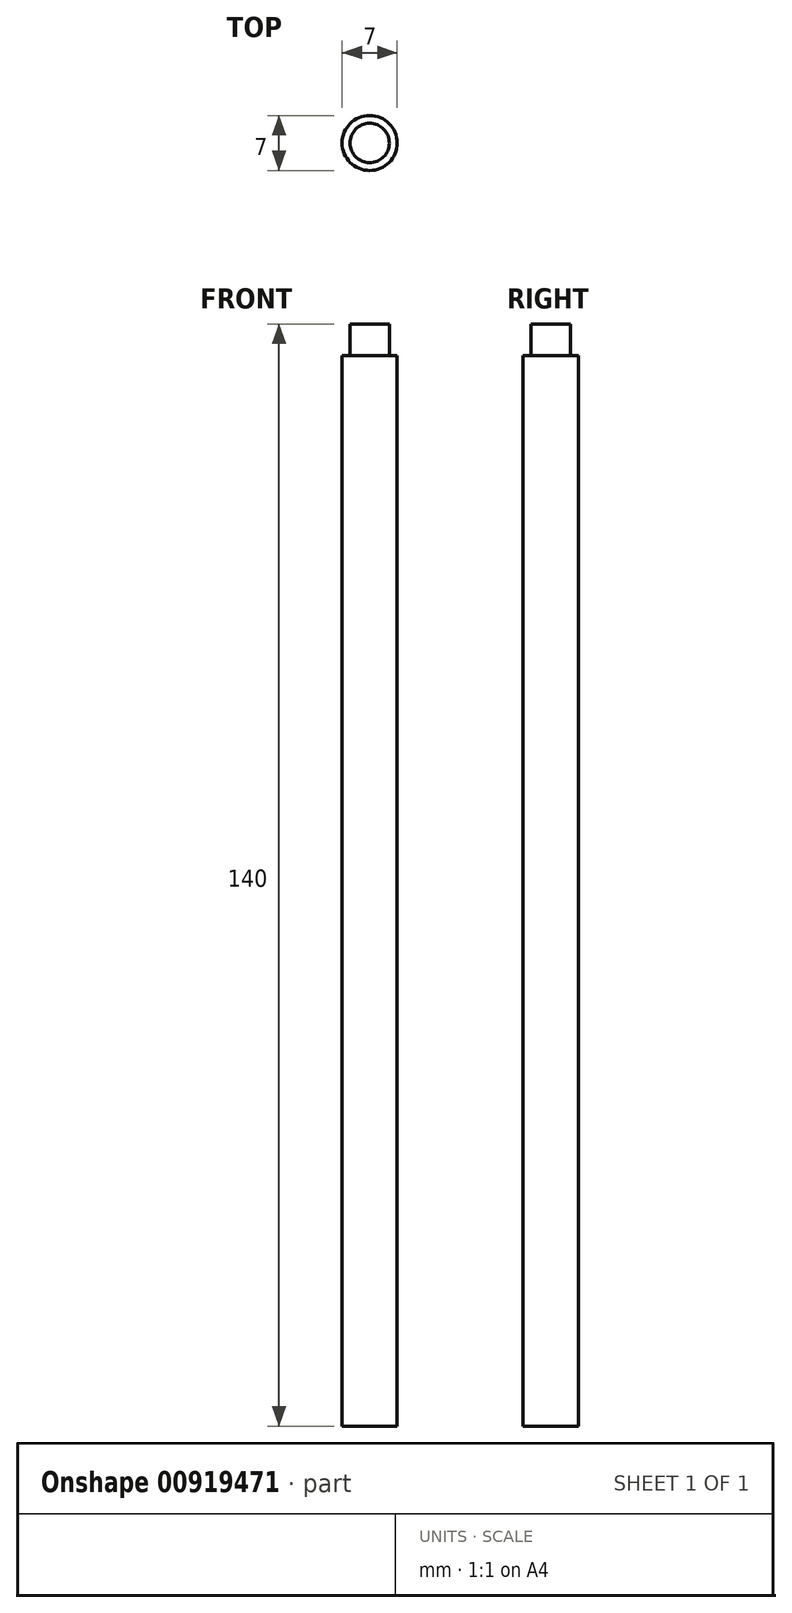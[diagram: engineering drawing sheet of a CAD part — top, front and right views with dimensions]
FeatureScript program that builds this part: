
annotation { "Feature Type Name" : "Feature", "Feature Type Description" : "" }
export const myFeature = defineFeature(function(context is Context, id is Id, definition is map)
    precondition{}
    {
        {
            var Q0;
            Q0=qCreatedBy(makeId("Top.planeOp"),FACE);
            var sketch = newSketch(context, id + "F0", { "sketchPlane" : qUnion([Q0])});
            skCircle(sketch, "E0", {"center": v(0, 0) * mm, "radius": 3.5 * mm});
            skSolve(sketch);
        }
        {
            var Q0;
            Q0 = qSketchRegion(id + "F0", true);
            extrude(context, id + "F1", {"entities" : qUnion([Q0]), "depth" : 140 * mm, "offsetDistance" : 25 * mm, "symmetric" : true});
        }
        {
            var Q0;
            Q0=makeQuery(id+"F1.opExtrude","CAP_FACE",FACE,{"disambiguationData":[OSD([sQuery(id+"F0.wireOp",EDGE,"E0")])],"isStart":false});
            var sketch = newSketch(context, id + "F2", { "sketchPlane" : qUnion([Q0])});
            skCircle(sketch, "E1", {"center": v(0, 0) * mm, "radius": 3.5 * mm});
            skCircle(sketch, "E2", {"center": v(0, 0) * mm, "radius": 2.5 * mm});
            skSolve(sketch);
        }
        {
            var Q0;
            Q0 = qSketchRegion(id + "F2", true);
            extrude(context, id + "F3", {"entities" : qUnion([Q0]), "operationType" : NewBodyOperationType.REMOVE, "oppositeDirection" : true, "depth" : 4 * mm, "offsetDistance" : 25 * mm});
        }
    });
